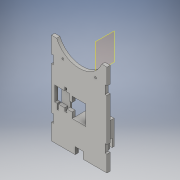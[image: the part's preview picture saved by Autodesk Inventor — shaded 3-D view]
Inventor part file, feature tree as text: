
AUTODESK INVENTOR PART (.ipt)
format: ipt  version: 2016 (Build 200138000, 138)  size: 333,312 bytes
history: native  units: in
note: dims shown in document units (in); Inventor stores cm internally (conversion verified against a paired STEP export)
features: reference x18, extrude x15, sketch x14, plane x2, projected_geometry x1
ambient origin geometry x8: Origin, YZ Plane, XZ Plane, XY Plane, X Axis, Y Axis, Z Axis, Center Point
bodies: Solid1 (feature_tree)
feature tree (50):
  extrude  "Extrusion1"  Depth=0.1969in TaperAngle=0.0deg
  extrude  "Extrusion2"  Depth=0.1969in TaperAngle=0.0deg
  extrude  "Extrusion3"  Depth=0.0787in
  extrude  "Extrusion4"  Depth=0.1969in TaperAngle=0.0deg
  extrude  "Extrusion6"  Depth=0.1969in
  extrude  "Extrusion7"  Depth=0.1969in TaperAngle=0.0deg
  extrude  "Extrusion8"  Depth=0.5in
  plane  "Work Plane1"
  extrude  "Extrusion18"  Depth=0.25in TaperAngle=0.0deg
  extrude  "Extrusion19"  Depth=0.15in
  extrude  "Extrusion21"  Depth=0.1181in
  plane  "Work Plane2"
  extrude  "Extrusion23"  Depth=1.0in TaperAngle=0.0deg
  extrude  "Extrusion24"  Depth=0.325in
  extrude  "Extrusion25"  Depth=0.0197in
  extrude  "Extrusion26"  Depth=0.3937in
  extrude  "Extrusion27"  Depth=0.3937in
  sketch  "Sketch1"  dims[d0=6.0in d1=0.1969in d2=0.0in]
  sketch  "Sketch2"  dims[d3=0.5906in d4=0.1969in d5=0.0in]
  reference  "Reference2"
  reference  "Reference3"
  sketch  "Sketch4"  dims[d6=3.0in d7=0.0787in]
  sketch  "Sketch6"  dims[d8=0.0787in d9=0.1969in d10=0.0in]
  sketch  "Sketch7"  dims[d11=0.1969in d12=0.1969in]
  sketch  "Sketch8"  dims[d13=0.1969in d14=0.1969in d15=0.0in]
  reference  "Reference6"
  reference  "Reference7"
  reference  "Reference8"
  reference  "Reference9"
  reference  "Reference10"
  reference  "Reference11"
  reference  "Reference12"
  reference  "Reference13"
  reference  "Reference14"
  reference  "Reference15"
  sketch  "Sketch18"  dims[d18=0.25in d19=0.5in]
  sketch  "Sketch20"  dims[d20=0.4in d21=0.0in d24=0.25in d25=0.0in]
  sketch  "Sketch22"  dims[d26=0.15in d27=0.1378in]
  sketch  "Sketch24"  dims[d28=0.0394in d29=0.1181in]
  reference  "Reference31"
  sketch  "Sketch25"  dims[d30=0.0394in d31=1.0in d32=0.0in]
  reference  "Reference32"
  reference  "Reference33"
  reference  "Reference34"
  sketch  "Sketch26"  dims[d33=0.02in d34=0.325in]
  reference  "Reference35"
  reference  "Reference36"
  sketch  "Sketch27"  dims[d35=0.02in d45=0.0197in]
  projected_geometry  "Projected Loop2"
  sketch  "Sketch28"  dims[d46=0.0197in d47=0.0197in d73=0.1181in d83=1.0in d84=0.5in d85=0.118in d86=1.0in d87=0.5in d88=0.118in d89=0.3937in d90=0.0in d91=0.8226in d92=0.0in d95=0.1in d96=0.0in d102=0.7in d103=1.063in d104=1.5in d106=0.7268in d107=0.8in d108=0.118in d109=0.5in d110=0.1in d111=1.2614in d112=0.0in d113=0.18in d114=0.18in d115=0.8in d116=0.3937in d117=0.0in d118=0.1181in d119=0.1181in d120=0.3937in d121=0.0in d122=0.0394in d123=0.0in d124=0.0394in d125=122.0in d126=0.0in]
